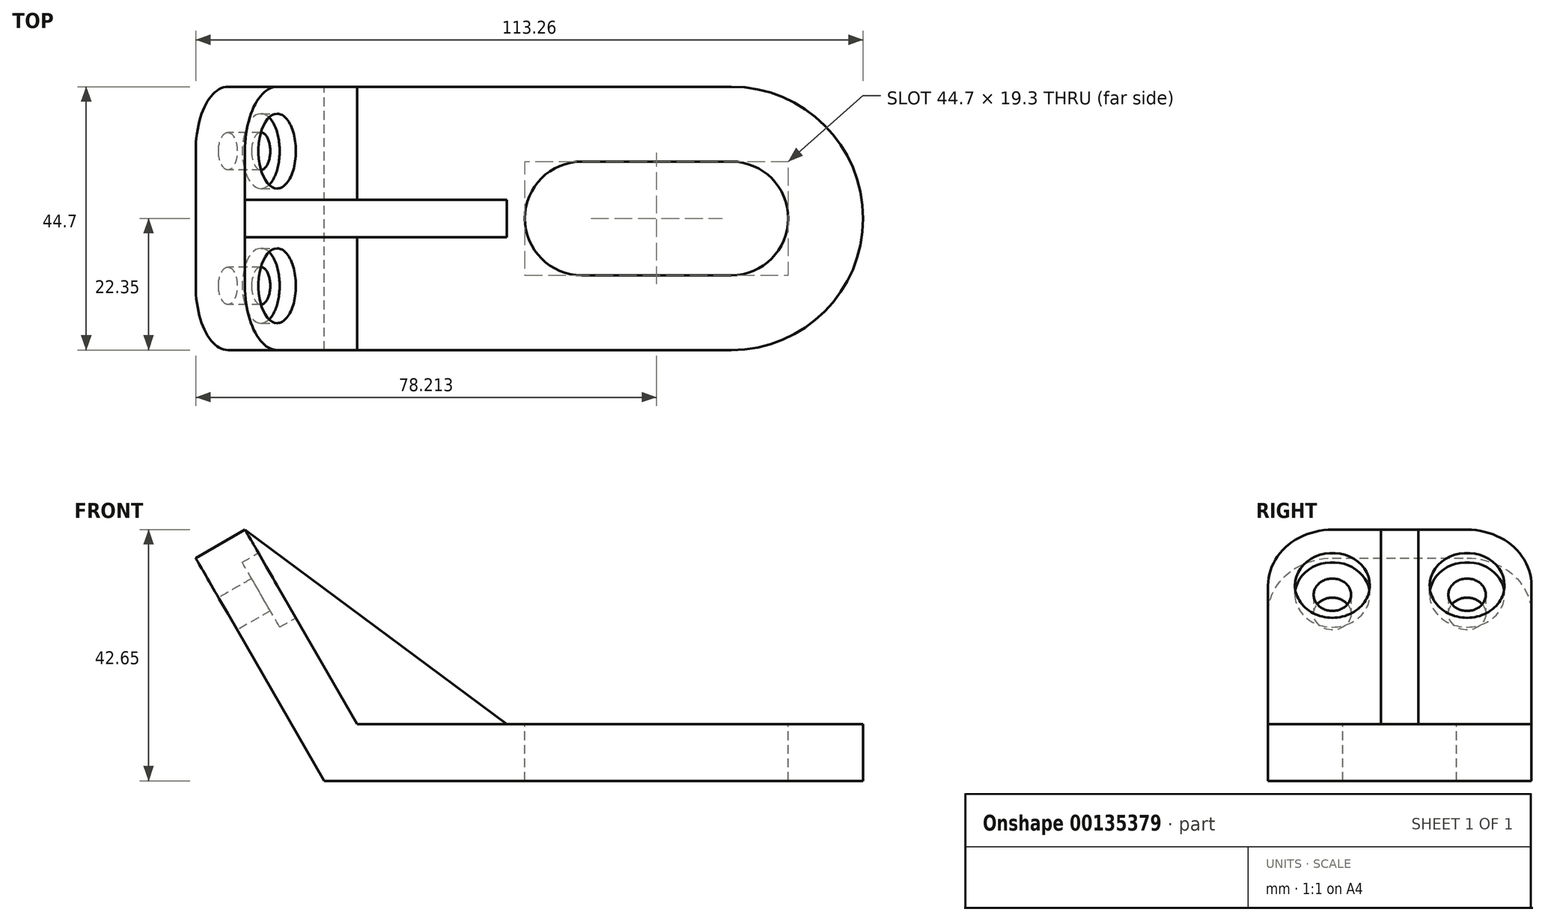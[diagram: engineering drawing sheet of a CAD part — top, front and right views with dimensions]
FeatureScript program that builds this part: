
annotation { "Feature Type Name" : "Feature", "Feature Type Description" : "" }
export const myFeature = defineFeature(function(context is Context, id is Id, definition is map)
    precondition{}
    {
        {
            var Q0;
            Q0=qCreatedBy(makeId("Front.planeOp"),FACE);
            var sketch = newSketch(context, id + "F0", { "sketchPlane" : qUnion([Q0])});
            skLineSegment(sketch, "E0", {"start": v(0, 0) * mm, "end": v(-21.84, 37.82) * mm});
            skLineSegment(sketch, "E1", {"start": v(-21.84, 37.82) * mm, "end": v(-13.48, 42.65) * mm});
            skLineSegment(sketch, "E2", {"start": v(-13.48, 42.65) * mm, "end": v(5.57, 9.65) * mm});
            skLineSegment(sketch, "E3", {"start": v(5.57, 9.65) * mm, "end": v(91.42, 9.65) * mm});
            skLineSegment(sketch, "E4", {"start": v(91.42, 9.65) * mm, "end": v(91.42, 0) * mm});
            skLineSegment(sketch, "E5", {"start": v(91.42, 0) * mm, "end": v(0, 0) * mm});
            skLineSegment(sketch, "E6", {"start": v(0, 0) * mm, "end": v(-13.22, 0) * mm, "construction": true});
            skLineSegment(sketch, "E7", {"start": v(-13.48, 42.65) * mm, "end": v(30.97, 9.65) * mm});
            skSolve(sketch);
        }
        {
            var Q0;
            Q0=makeQuery(id+"F0.imprint","IMPRINT",FACE,{"disambiguationData":[TD([[makeQuery(id+"F0.imprint","IMPRINT",EDGE,{"derivedFrom":sQuery(id+"F0.wireOp",EDGE,"E0")}),-1.0]])]});
            extrude(context, id + "F1", {"entities" : qUnion([Q0]), "endBound" : BoundingType.SYMMETRIC, "depth" : 44.7 * mm});
        }
        {
            var Q0;
            {var subQ0=sQuery(id+"F0.wireOp",EDGE,"E2");Q0=makeQuery(id+"F0.imprint","IMPRINT",FACE,{"disambiguationData":[TD([[makeQuery(id+"F0.imprint","IMPRINT",EDGE,{"derivedFrom":subQ0}),1.0]])]});}
            extrude(context, id + "F2", {"entities" : qUnion([Q0]), "operationType" : NewBodyOperationType.ADD, "endBound" : BoundingType.SYMMETRIC, "depth" : 6.35 * mm});
        }
        {
            var Q0;
            Q0=makeQuery(id+"F1.opExtrude","SWEPT_FACE",FACE,{"disambiguationData":[OSD([sQuery(id+"F0.wireOp",EDGE,"E3")])]});
            var sketch = newSketch(context, id + "F3", { "sketchPlane" : qUnion([Q0])});
            skLineSegment(sketch, "E8", {"start": v(5.57, 0) * mm, "end": v(43.67, 0) * mm, "construction": true});
            skLineSegment(sketch, "E9", {"start": v(43.67, 0) * mm, "end": v(69.07, 0) * mm, "construction": true});
            skArc(sketch, "E10", {"start": v(69.07, -9.65) * mm, "mid": v(78.72, 0) * mm, "end": v(69.07, 9.65) * mm});
            skArc(sketch, "E11", {"start": v(43.67, 9.65) * mm, "mid": v(34.02, 0) * mm, "end": v(43.67, -9.65) * mm});
            skLineSegment(sketch, "E12", {"start": v(43.67, 9.65) * mm, "end": v(69.07, 9.65) * mm});
            skLineSegment(sketch, "E13", {"start": v(69.07, -9.65) * mm, "end": v(43.67, -9.65) * mm});
            skCircle(sketch, "E14", {"center": v(69.07, 0) * mm, "radius": 22.35 * mm});
            skLineSegment(sketch, "E15", {"start": v(69.07, 0) * mm, "end": v(69.07, 22.35) * mm, "construction": true});
            skLineSegment(sketch, "E16", {"start": v(69.07, 0) * mm, "end": v(69.07, -22.35) * mm, "construction": true});
            skSolve(sketch);
        }
        {
            var Q0;
            {var subQ0=sQuery(id+"F3.wireOp",EDGE,"E14");var subQ1=sQuery(id+"F0.wireOp",EDGE,"E3");var subQ2=makeQuery(id+"F1.opExtrude","CAP_EDGE",EDGE,{"disambiguationData":[OSD([subQ1])],"isStart":true});var subQ3=makeQuery(id+"F3.imprint","INTERSECT",VERTEX,{"derivedFrom":[subQ2,subQ0]});Q0=makeQuery(id+"F3.imprint","IMPRINT",FACE,{"disambiguationData":[TD([[makeQuery(id+"F3.imprint","IMPRINT",EDGE,{"disambiguationData":[TD([[subQ3,1.0]])],"derivedFrom":subQ0}),-1.0]])]});}
            var Q1;
            {var subQ0=sQuery(id+"F3.wireOp",EDGE,"E14");var subQ1=sQuery(id+"F0.wireOp",EDGE,"E3");var subQ4=makeQuery(id+"F1.opExtrude","CAP_EDGE",EDGE,{"disambiguationData":[OSD([subQ1])],"isStart":false});var subQ5=makeQuery(id+"F3.imprint","INTERSECT",VERTEX,{"derivedFrom":[subQ4,subQ0]});Q1=makeQuery(id+"F3.imprint","IMPRINT",FACE,{"disambiguationData":[TD([[makeQuery(id+"F3.imprint","IMPRINT",EDGE,{"disambiguationData":[TD([[subQ5,-1.0]])],"derivedFrom":subQ0}),-1.0]])]});}
            var Q2;
            {var subQ0=sQuery(id+"F3.wireOp",EDGE,"E10");Q2=makeQuery(id+"F3.imprint","IMPRINT",FACE,{"disambiguationData":[TD([[makeQuery(id+"F3.imprint","IMPRINT",EDGE,{"derivedFrom":subQ0}),1.0]])]});}
            var Q3;
            {var subQ0=sQuery(id+"F3.wireOp",EDGE,"E11");Q3=makeQuery(id+"F3.imprint","IMPRINT",FACE,{"disambiguationData":[TD([[makeQuery(id+"F3.imprint","IMPRINT",EDGE,{"derivedFrom":subQ0}),1.0]])]});}
            extrude(context, id + "F4", {"entities" : qUnion([Q0, Q1, Q2, Q3]), "operationType" : NewBodyOperationType.REMOVE, "oppositeDirection" : true, "depth" : 25.4 * mm});
        }
        {
            var Q0;
            Q0=makeQuery(id+"F1.opExtrude","SWEPT_FACE",FACE,{"disambiguationData":[OSD([sQuery(id+"F0.wireOp",EDGE,"E0")])]});
            var sketch = newSketch(context, id + "F5", { "sketchPlane" : qUnion([Q0])});
            skLineSegment(sketch, "E17.0", {"start": v(22.35, 43.67) * mm, "end": v(-22.35, 43.67) * mm});
            skLineSegment(sketch, "E18.0", {"start": v(-22.35, 0) * mm, "end": v(-22.35, 43.67) * mm});
            skLineSegment(sketch, "E19.0", {"start": v(22.35, 0) * mm, "end": v(22.35, 43.67) * mm});
            skLineSegment(sketch, "E20.0", {"start": v(22.35, 0) * mm, "end": v(-22.35, 0) * mm});
            skLineSegment(sketch, "E21", {"start": v(-22.35, 32.75) * mm, "end": v(22.35, 32.75) * mm, "construction": true});
            skLineSegment(sketch, "E22", {"start": v(-11.43, 43.67) * mm, "end": v(-11.43, 32.75) * mm, "construction": true});
            skLineSegment(sketch, "E23", {"start": v(11.43, 43.67) * mm, "end": v(11.43, 32.75) * mm, "construction": true});
            skCircle(sketch, "E24", {"center": v(-11.43, 32.75) * mm, "radius": 6.35 * mm});
            skCircle(sketch, "E25", {"center": v(-11.43, 32.75) * mm, "radius": 3.18 * mm});
            skCircle(sketch, "E26", {"center": v(11.43, 32.75) * mm, "radius": 6.35 * mm});
            skCircle(sketch, "E27", {"center": v(11.43, 32.75) * mm, "radius": 3.18 * mm});
            skSolve(sketch);
        }
        {
            var Q0;
            {var subQ0=sQuery(id+"F0.wireOp",EDGE,"E7");var subQ1=sQuery(id+"F0.wireOp",EDGE,"E3");var subQ2=sQuery(id+"F0.wireOp",EDGE,"E2");Q0=makeQuery(id+"F2.boolean.opBoolean","SPLIT",FACE,{"disambiguationData":[TD([makeQuery(id+"F2.opExtrude","CAP_FACE",FACE,{"disambiguationData":[OSD([subQ2,subQ1,subQ0])],"isStart":false})])],"derivedFrom":makeQuery(id+"F1.opExtrude","SWEPT_FACE",FACE,{"disambiguationData":[OSD([subQ2])]})});}
            var sketch = newSketch(context, id + "F6", { "sketchPlane" : qUnion([Q0])});
            skCircle(sketch, "E28.0", {"center": v(11.43, 32.75) * mm, "radius": 6.35 * mm});
            skSolve(sketch);
        }
        {
            var Q0;
            Q0 = qSketchRegion(id + "F6", true);
            extrude(context, id + "F7", {"entities" : qUnion([Q0]), "operationType" : NewBodyOperationType.REMOVE, "oppositeDirection" : true, "depth" : 3.17 * mm});
        }
        {
            var Q0;
            {var subQ0=sQuery(id+"F0.wireOp",EDGE,"E7");var subQ1=sQuery(id+"F0.wireOp",EDGE,"E3");var subQ2=sQuery(id+"F0.wireOp",EDGE,"E2");Q0=makeQuery(id+"F2.boolean.opBoolean","SPLIT",FACE,{"disambiguationData":[TD([makeQuery(id+"F2.opExtrude","CAP_FACE",FACE,{"disambiguationData":[OSD([subQ2,subQ1,subQ0])],"isStart":false})])],"derivedFrom":makeQuery(id+"F1.opExtrude","SWEPT_FACE",FACE,{"disambiguationData":[OSD([subQ2])]})});}
            var sketch = newSketch(context, id + "F8", { "sketchPlane" : qUnion([Q0])});
            skCircle(sketch, "E29.0", {"center": v(-11.43, 32.75) * mm, "radius": 6.35 * mm});
            skSolve(sketch);
        }
        {
            var Q0;
            Q0 = qSketchRegion(id + "F8", true);
            extrude(context, id + "F9", {"entities" : qUnion([Q0]), "operationType" : NewBodyOperationType.REMOVE, "oppositeDirection" : true, "depth" : 3.17 * mm});
        }
        {
            var Q0;
            Q0=makeQuery(id+"F5.imprint","IMPRINT",FACE,{"disambiguationData":[TD([[makeQuery(id+"F5.imprint","IMPRINT",EDGE,{"derivedFrom":sQuery(id+"F5.wireOp",EDGE,"E25")}),1.0]])]});
            var Q1;
            Q1=makeQuery(id+"F5.imprint","IMPRINT",FACE,{"disambiguationData":[TD([[makeQuery(id+"F5.imprint","IMPRINT",EDGE,{"derivedFrom":sQuery(id+"F5.wireOp",EDGE,"E27")}),1.0]])]});
            extrude(context, id + "F10", {"entities" : qUnion([Q0, Q1]), "operationType" : NewBodyOperationType.REMOVE, "oppositeDirection" : true, "depth" : 25.4 * mm});
        }
        {
            var Q0;
            Q0=makeQuery(id+"F1.opExtrude","CAP_EDGE",EDGE,{"disambiguationData":[OSD([sQuery(id+"F0.wireOp",EDGE,"E1")])],"isStart":false});
            var Q1;
            Q1=makeQuery(id+"F1.opExtrude","CAP_EDGE",EDGE,{"disambiguationData":[OSD([sQuery(id+"F0.wireOp",EDGE,"E1")])],"isStart":true});
            fillet(context, id + "F11", {"entities" : qUnion([Q0, Q1]), "radius" : 10.92 * mm, "tangentPropagation" : true, "allowEdgeOverflow" : false});
        }
    });
